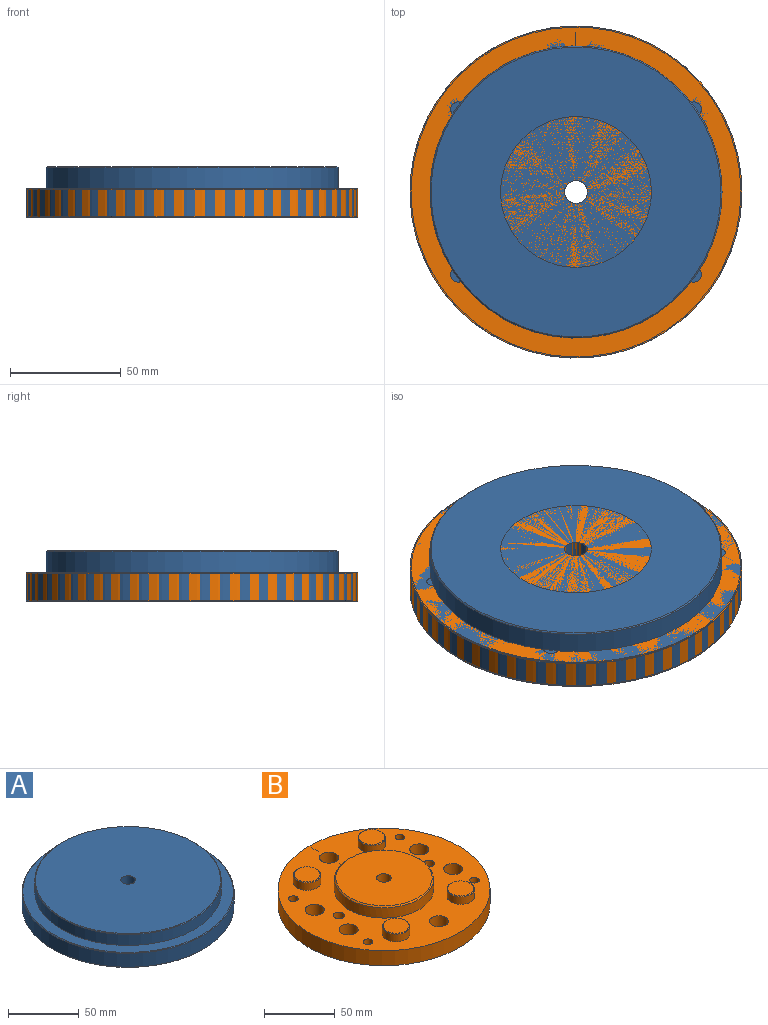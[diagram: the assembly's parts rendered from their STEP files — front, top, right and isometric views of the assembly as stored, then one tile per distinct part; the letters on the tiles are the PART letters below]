
ASSEMBLY  parts=2 mates=1
PART A: 9 faces, bbox 150x150x23 mm
  f0: cylinder r=75mm len=150mm, axis (0,0,1), area 5654.9mm2, adj f6,f7
  f1: plane 149x149mm, normal (0,0,-1), area 17353.3mm2, adj f6,f8
  f2: cylinder r=66mm len=132mm, axis (0,0,1), area 3939.6mm2, adj f3,f5
  f3: plane 149x149mm, normal (0,0,1), area 3751.8mm2, adj f2,f7
  f4: plane 131x131mm, normal (0,0,1), area 13394.9mm2, adj f5,f8
  f5: cone r=65.5mm half-angle=45deg, axis (0,0,-1), area 292.1mm2, adj f2,f4
  f6: cone r=75mm half-angle=45deg, axis (0,0,1), area 332.1mm2, adj f0,f1
  f7: cone r=74.5mm half-angle=45deg, axis (0,0,-1), area 332.1mm2, adj f0,f3
  f8: cylinder r=5.15mm len=23mm, axis (0,0,1), area 744.2mm2, adj f1,f4
PART B: 40 faces, bbox 150x150x23 mm
  f0: plane 150x150mm, normal (0,0,-1), area 16483.2mm2, adj f2,f3,f4,f5,f6,f7,f8,f9
  f1: plane 150x150mm, normal (0,0,1), area 11525mm2, adj f2,f3,f4,f5,f6,f7,f8,f9
  f2: cylinder r=10.69mm len=13mm, axis (0,0,1), area 0.3mm2, adj f0,f1,f3,f11
  f3: plane 13x7.25mm, normal (1,0,0), area 94.3mm2, adj f0,f1,f2,f4
  f4: cylinder r=37.06mm len=13mm, axis (0,0,1), area 0.3mm2, adj f0,f1,f3,f11
  f5: cylinder r=72.14mm len=13mm, axis (0,0,1), area 0.1mm2, adj f0,f1,f6,f10
  f6: plane 13x6.45mm, normal (1,0,0), area 83.8mm2, adj f0,f1,f5,f7
  f7: cylinder r=10.69mm len=13mm, axis (0,0,1), area 0.3mm2, adj f0,f1,f6,f8
  f8: plane 13x6.45mm, normal (-1,0,0), area 83.8mm2, adj f0,f1,f7,f10
  f9: cylinder r=75mm len=150mm, axis (0,0,1), area 6126.1mm2, adj f0,f1
  f10: cylinder r=72.14mm len=13mm, axis (0,0,1), area 0.1mm2, adj f0,f1,f5,f8
  f11: plane 13x7.25mm, normal (-1,0,0), area 94.3mm2, adj f0,f1,f2,f4
  f12: cylinder r=9.69mm len=19.38mm, axis (0,0,-1), area 395.7mm2, adj f1,f20
  f13: plane 18.38x18.38mm, normal (0,0,1), area 265.3mm2, adj f20
  f14: cylinder r=9.69mm len=19.38mm, axis (0,0,-1), area 395.7mm2, adj f1,f21
  f15: plane 18.38x18.38mm, normal (0,0,1), area 265.3mm2, adj f21
  f16: cylinder r=9.69mm len=19.38mm, axis (0,0,-1), area 395.7mm2, adj f1,f22
  f17: plane 18.38x18.38mm, normal (0,0,1), area 265.3mm2, adj f22
  f18: cylinder r=9.69mm len=19.38mm, axis (0,0,-1), area 395.7mm2, adj f1,f23
  f19: plane 18.38x18.38mm, normal (0,0,1), area 265.3mm2, adj f23
  f20: cone r=9.19mm half-angle=45deg, axis (0,0,-1), area 41.9mm2, adj f12,f13
  f21: cone r=9.19mm half-angle=45deg, axis (0,0,-1), area 41.9mm2, adj f14,f15
  f22: cone r=9.19mm half-angle=45deg, axis (0,0,-1), area 41.9mm2, adj f16,f17
  f23: cone r=9.19mm half-angle=45deg, axis (0,0,-1), area 41.9mm2, adj f18,f19
  f24: cylinder r=6.75mm len=13.5mm, axis (0,0,1), area 551.3mm2, adj f0,f1
  f25: cylinder r=6.75mm len=13.5mm, axis (0,0,1), area 551.3mm2, adj f0,f1
  f26: cylinder r=6.75mm len=13.5mm, axis (0,0,1), area 551.3mm2, adj f0,f1
  f27: cylinder r=6.75mm len=13.5mm, axis (0,0,1), area 551.3mm2, adj f0,f1
  f28: cylinder r=6.75mm len=13.5mm, axis (0,0,1), area 551.3mm2, adj f0,f1
  f29: cylinder r=6.75mm len=13.5mm, axis (0,0,1), area 551.3mm2, adj f0,f1
  f30: cylinder r=4mm len=13mm, axis (0,0,1), area 326.7mm2, adj f0,f1
  f31: cylinder r=4mm len=13mm, axis (0,0,1), area 326.7mm2, adj f0,f1
  f32: cylinder r=3.4mm len=13mm, axis (0,0,1), area 277.7mm2, adj f0,f1
  f33: cylinder r=3.4mm len=13mm, axis (0,0,1), area 277.7mm2, adj f0,f1
  f34: cylinder r=3.4mm len=13mm, axis (0,0,1), area 277.7mm2, adj f0,f1
  f35: cylinder r=3.4mm len=13mm, axis (0,0,1), area 277.7mm2, adj f0,f1
  f36: cylinder r=35.06mm len=70.12mm, axis (0,0,-1), area 1982.6mm2, adj f1,f38
  f37: plane 68.12x68.12mm, normal (0,0,1), area 3561.2mm2, adj f38,f39
  f38: cone r=34.06mm half-angle=45deg, axis (0,0,-1), area 307.1mm2, adj f36,f37
  f39: cylinder r=5.15mm len=23mm, axis (0,0,1), area 744.2mm2, adj f0,f37
PLACE A at identity
PLACE B t=(0,0,-10)mm
MATE fastened A.f2 <-> B.f9  axis (0,0,1) through (0,0,0)mm
